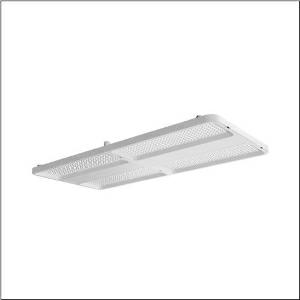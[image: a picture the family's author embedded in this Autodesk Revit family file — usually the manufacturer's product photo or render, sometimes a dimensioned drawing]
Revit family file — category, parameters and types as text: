
# Revit family: highbay_21_maxi_52hn11db4mda02
name_source: partatom
category: Lighting Fixtures
units: mm (PartAtom-declared; Revit-internal decimal feet)

## family parameters
Cut with Voids When Loaded = No
Host = Face
Light Source = No
Part Type = Normal
Room Calculation Point = No
Round Connector Dimension = Use Diameter
Shared = No

## types (1)
- --- (1 x LED, 28000 lm, 144.5 W, 4000K)
    Apparent Load = 144 VA
    CIE Flux Codes = 89 97 99 100 100
    Color Rendering = 80
    Color Temperature = 4000K
    Default Elevation = 1800 mm
    Description = high bay luminaire Highbay 21 maxi; direct symmetric narrow distribution, light control with lens of PMMA; UGR ≤ 19 (X = 4H | Y = 8H | S = 0.25H | reflection values 70/50/20); luminous flux: 28.000lm; light colour: 840, colour temperature: 4000K, MacAdam ≤ 3 SDCM (initial), colour rendering: CRI > 80; luminous efficacy: 193,8lm/W; rated service life: 75.000h (L80/B50) at AT= ta max; control: Bluetooth® Mesh; for wireless networking: Node luminaire for setting up a local control solution without a higher-level application controller, intelligence completely in the luminaire; no control line such as DALI between the Node multi-sensor luminaires and Nodes is required, wireless integration of other Node luminaires and Node multi-sensor luminaires into the network is possible; number of Node luminaires in the project can be expanded as required, network sizes > 300 Nodes can be realized; can also be connected to lighting or building automation via various gateways upon request; integrated DALI2 ECG provides luminaire data (according to IEC62386, Part 251), energy data (Part 252), and monitoring and analytics data (Part 253) to higher-level systems for further processing; luminaire connection: terminal, 5-pole, max. 2.5mm² (cable entry for one cable, Ø 8.5..16mm); mains connection: 230..240V, AC 50/60Hz; connected load: 144,5W; protection rating (complete): IP66; insulation class (complete): insulation class I (protective earthing); protection symbol: D; impact resistance: IK08; certification: CE, ENEC, VDE, UKCA; internal wiring halogen-free; luminaire corresponds to IFS (International Featured Standards) requirements for safety and quality in the food industry; LABS conformity tested according to VDMA 24364:2018-05; housing frame of high-performance plastic PA6, matt traffic white (RAL 9016); cover of PMMA; dimension (LxWxH): 946 x 442 x 72mm; permissible operating ambient temperature: -20..+45°C (reducing of maximum allowable ambient temperature of 5°C with ceiling mounting); packaging unit: 1 piece; (delivery without accessories; please order mounting accessories separately)
    Height = 72 mm  [stored 0.23622 ft]
    Lamp = 1 x LED
    Lamp Light Flux = 28000 lm
    Lamp Power = 144.5 W
    Lamp count = 1
    Length = 946 mm
    Luminous efficacy = 194 lm/W
    Manufacturer = Siteco
    ModVariant = No
    Model = 52HN11DB4MDA02
    Mounting Place = Ceiling
    Mounting Type = Pendant
    Number of Poles = 1
    OnlyDefault = Yes
    Power Factor = 1
    Product Name = Highbay 21 maxi
    Product group = high bay luminaire
    ProductGroupID = 901
    Protection Class = Protection class I
    Protection Degree = IP 66
    RLX_Detail_Level = 1
    RLX_Emergency_Light_Flux = 0 lm
    RLX_Emergency_Type = 0
    RLX_Emergency_Type_DB = No
    RlxData = <blob elided: 128893 chars, md5=89a56894>
    Socket = socket
    Standby Power = 0 W
    System Light Flux = 28000 lm
    System Power = 144 W
    Type Comments = factory setting: luminous flux: 100 % | dim-lin: 254 | 668 mA
    Type Image = l_1363244.jpg
    URL = http://relux.com
    VarID = @adj_010317
    Voltage = 0 V
    Weight = 0.00 kg
    Width = 442 mm

note: [stored X ft] marks values corroborated as IEEE doubles in the binary element streams (Revit-internal decimal feet)

## geometry (parser evidence)
native form markers: Blend x4, Sweep x9
no freeform markers — native parametric forms only
